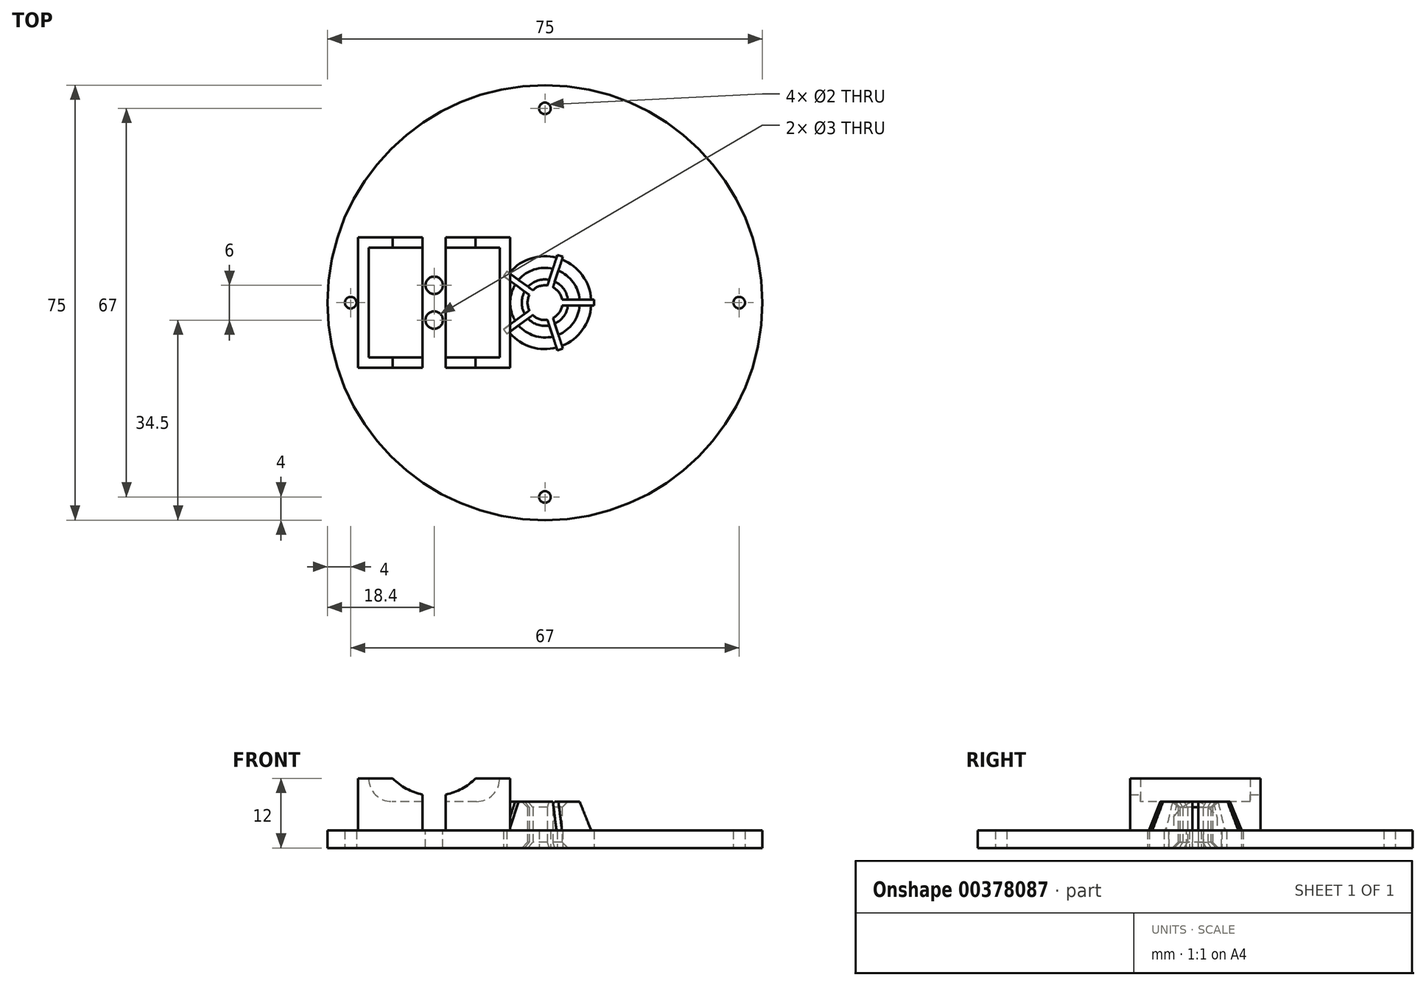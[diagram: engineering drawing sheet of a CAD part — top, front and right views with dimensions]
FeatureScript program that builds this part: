
annotation { "Feature Type Name" : "Feature", "Feature Type Description" : "" }
export const myFeature = defineFeature(function(context is Context, id is Id, definition is map)
    precondition{}
    {
        {
            var Q0;
            Q0=qCreatedBy(makeId("Top.planeOp"),FACE);
            var sketch = newSketch(context, id + "F0", { "sketchPlane" : qUnion([Q0])});
            skCircle(sketch, "E0", {"center": v(0, 0) * mm, "radius": 37.5 * mm});
            skCircle(sketch, "E1", {"center": v(0, 0) * mm, "radius": 3 * mm});
            skLineSegment(sketch, "E2.bottom", {"start": v(-8, 9.25) * mm, "end": v(-30.2, 9.25) * mm, "construction": true});
            skLineSegment(sketch, "E2.top", {"start": v(-8, -9.25) * mm, "end": v(-30.2, -9.25) * mm, "construction": true});
            skLineSegment(sketch, "E2.left", {"start": v(-8, 9.25) * mm, "end": v(-8, -9.25) * mm, "construction": true});
            skLineSegment(sketch, "E2.right", {"start": v(-30.2, 9.25) * mm, "end": v(-30.2, -9.25) * mm, "construction": true});
            skPoint(sketch, "E2.middle", {"position": v(-19.1, 0) * mm});
            skLineSegment(sketch, "E3", {"start": v(-3, 37.38) * mm, "end": v(-3, -37.38) * mm, "construction": true});
            skCircle(sketch, "E4", {"center": v(0, 0) * mm, "radius": 33.5 * mm, "construction": true});
            skCircle(sketch, "E5", {"center": v(33.5, 0) * mm, "radius": 1 * mm});
            skCircle(sketch, "E6.1.0", {"center": v(0, -33.5) * mm, "radius": 1 * mm});
            skCircle(sketch, "E6.2.0", {"center": v(-33.5, 0) * mm, "radius": 1 * mm});
            skCircle(sketch, "E6.3.0", {"center": v(0, 33.5) * mm, "radius": 1 * mm});
            skLineSegment(sketch, "E6.anchor1", {"start": v(0, 0) * mm, "end": v(33.5, 0) * mm, "construction": true});
            skLineSegment(sketch, "E6.anchor2", {"start": v(0, 0) * mm, "end": v(0, 33.5) * mm, "construction": true});
            skSolve(sketch);
        }
        {
            var Q0;
            Q0=makeQuery(id+"F0.imprint","IMPRINT",FACE,{"disambiguationData":[TD([[makeQuery(id+"F0.imprint","IMPRINT",EDGE,{"derivedFrom":sQuery(id+"F0.wireOp",EDGE,"E1")}),-1.0]])]});
            extrude(context, id + "F1", {"entities" : qUnion([Q0]), "depth" : 3 * mm});
        }
        {
            var Q0;
            Q0=makeQuery(id+"F1.opExtrude","CAP_FACE",FACE,{"disambiguationData":[OSD([sQuery(id+"F0.wireOp",EDGE,"E1"),sQuery(id+"F0.wireOp",EDGE,"E5"),sQuery(id+"F0.wireOp",EDGE,"E6.1.0"),sQuery(id+"F0.wireOp",EDGE,"E6.2.0"),sQuery(id+"F0.wireOp",EDGE,"E6.3.0"),sQuery(id+"F0.wireOp",EDGE,"E0")])],"isStart":false});
            var sketch = newSketch(context, id + "F2", { "sketchPlane" : qUnion([Q0])});
            skCircle(sketch, "E7", {"center": v(0, 0) * mm, "radius": 8 * mm});
            skCircle(sketch, "E8", {"center": v(0, 0) * mm, "radius": 3 * mm});
            skSolve(sketch);
        }
        {
            var Q0;
            Q0=makeQuery(id+"F2.imprint","IMPRINT",FACE,{"disambiguationData":[TD([[makeQuery(id+"F2.imprint","IMPRINT",EDGE,{"derivedFrom":sQuery(id+"F2.wireOp",EDGE,"E7")}),1.0]])]});
            extrude(context, id + "F3", {"entities" : qUnion([Q0]), "operationType" : NewBodyOperationType.ADD, "depth" : 5 * mm});
        }
        {
            var Q0;
            Q0=makeQuery(id+"F3.opExtrude","CAP_EDGE",EDGE,{"disambiguationData":[OSD([sQuery(id+"F2.wireOp",EDGE,"E7")])],"isStart":false});
            chamfer(context, id + "F4", {"entities" : qUnion([Q0]), "chamferType" : ChamferType.TWO_OFFSETS, "width1" : 2 * mm, "oppositeDirection" : false, "width2" : 5 * mm, "tangentPropagation" : true});
        }
        {
            var Q0;
            Q0=makeQuery(id+"F3.boolean.opBoolean","MERGE",FACE,{"derivedFrom":[makeQuery(id+"F1.opExtrude","SWEPT_FACE",FACE,{"disambiguationData":[OSD([sQuery(id+"F0.wireOp",EDGE,"E1")])]}),makeQuery(id+"F3.opExtrude","SWEPT_FACE",FACE,{"disambiguationData":[OSD([sQuery(id+"F2.wireOp",EDGE,"E8")])]})]});
            chamfer(context, id + "F5", {"entities" : qUnion([Q0]), "width" : 1 * mm, "tangentPropagation" : true});
        }
        {
            var Q0;
            Q0=makeQuery(id+"F1.opExtrude","CAP_FACE",FACE,{"disambiguationData":[OSD([sQuery(id+"F0.wireOp",EDGE,"E1"),sQuery(id+"F0.wireOp",EDGE,"E5"),sQuery(id+"F0.wireOp",EDGE,"E6.1.0"),sQuery(id+"F0.wireOp",EDGE,"E6.2.0"),sQuery(id+"F0.wireOp",EDGE,"E6.3.0"),sQuery(id+"F0.wireOp",EDGE,"E0")])],"isStart":true});
            var sketch = newSketch(context, id + "F6", { "sketchPlane" : qUnion([Q0])});
            skLineSegment(sketch, "E9.bottom", {"start": v(8.5, 0.5) * mm, "end": v(2.5, 0.5) * mm});
            skLineSegment(sketch, "E9.top", {"start": v(8.5, -0.5) * mm, "end": v(2.5, -0.5) * mm});
            skLineSegment(sketch, "E9.left", {"start": v(8.5, 0.5) * mm, "end": v(8.5, -0.5) * mm});
            skLineSegment(sketch, "E9.right", {"start": v(2.5, 0.5) * mm, "end": v(2.5, -0.5) * mm});
            skPoint(sketch, "E9.middle", {"position": v(5.5, 0) * mm});
            skLineSegment(sketch, "E10.1.0", {"start": v(3.1, 7.93) * mm, "end": v(1.25, 2.22) * mm});
            skLineSegment(sketch, "E10.1.1", {"start": v(2.15, 8.24) * mm, "end": v(3.1, 7.93) * mm});
            skLineSegment(sketch, "E10.1.2", {"start": v(2.15, 8.24) * mm, "end": v(0.3, 2.53) * mm});
            skLineSegment(sketch, "E10.1.3", {"start": v(0.3, 2.53) * mm, "end": v(1.25, 2.22) * mm});
            skLineSegment(sketch, "E10.2.0", {"start": v(-6.58, 5.4) * mm, "end": v(-1.73, 1.87) * mm});
            skLineSegment(sketch, "E10.2.1", {"start": v(-7.17, 4.6) * mm, "end": v(-6.58, 5.4) * mm});
            skLineSegment(sketch, "E10.2.2", {"start": v(-7.17, 4.6) * mm, "end": v(-2.32, 1.06) * mm});
            skLineSegment(sketch, "E10.2.3", {"start": v(-2.32, 1.06) * mm, "end": v(-1.73, 1.87) * mm});
            skLineSegment(sketch, "E10.3.0", {"start": v(-7.17, -4.6) * mm, "end": v(-2.32, -1.06) * mm});
            skLineSegment(sketch, "E10.3.1", {"start": v(-6.58, -5.4) * mm, "end": v(-7.17, -4.6) * mm});
            skLineSegment(sketch, "E10.3.2", {"start": v(-6.58, -5.4) * mm, "end": v(-1.73, -1.87) * mm});
            skLineSegment(sketch, "E10.3.3", {"start": v(-1.73, -1.87) * mm, "end": v(-2.32, -1.06) * mm});
            skLineSegment(sketch, "E10.4.0", {"start": v(2.15, -8.24) * mm, "end": v(0.3, -2.53) * mm});
            skLineSegment(sketch, "E10.4.1", {"start": v(3.1, -7.93) * mm, "end": v(2.15, -8.24) * mm});
            skLineSegment(sketch, "E10.4.2", {"start": v(3.1, -7.93) * mm, "end": v(1.25, -2.22) * mm});
            skLineSegment(sketch, "E10.4.3", {"start": v(1.25, -2.22) * mm, "end": v(0.3, -2.53) * mm});
            skPoint(sketch, "E10.center", {"position": v(0, 0) * mm});
            skSolve(sketch);
        }
        {
            var Q0;
            {var subQ0=sQuery(id+"F6.wireOp",EDGE,"E10.2.3");Q0=makeQuery(id+"F6.imprint","IMPRINT",FACE,{"disambiguationData":[TD([[makeQuery(id+"F6.imprint","IMPRINT",EDGE,{"derivedFrom":subQ0}),1.0]])]});}
            var Q1;
            {var subQ0=sQuery(id+"F6.wireOp",EDGE,"E10.1.3");Q1=makeQuery(id+"F6.imprint","IMPRINT",FACE,{"disambiguationData":[TD([[makeQuery(id+"F6.imprint","IMPRINT",EDGE,{"derivedFrom":subQ0}),1.0]])]});}
            var Q2;
            {var subQ0=sQuery(id+"F6.wireOp",EDGE,"E10.1.1");Q2=makeQuery(id+"F6.imprint","IMPRINT",FACE,{"disambiguationData":[TD([[makeQuery(id+"F6.imprint","IMPRINT",EDGE,{"derivedFrom":subQ0}),-1.0]])]});}
            var Q3;
            {var subQ0=sQuery(id+"F6.wireOp",EDGE,"E9.left");Q3=makeQuery(id+"F6.imprint","IMPRINT",FACE,{"disambiguationData":[TD([[makeQuery(id+"F6.imprint","IMPRINT",EDGE,{"derivedFrom":subQ0}),-1.0]])]});}
            var Q4;
            {var subQ0=sQuery(id+"F6.wireOp",EDGE,"E10.4.1");Q4=makeQuery(id+"F6.imprint","IMPRINT",FACE,{"disambiguationData":[TD([[makeQuery(id+"F6.imprint","IMPRINT",EDGE,{"derivedFrom":subQ0}),-1.0]])]});}
            var Q5;
            {var subQ0=sQuery(id+"F6.wireOp",EDGE,"E9.right");Q5=makeQuery(id+"F6.imprint","IMPRINT",FACE,{"disambiguationData":[TD([[makeQuery(id+"F6.imprint","IMPRINT",EDGE,{"derivedFrom":subQ0}),1.0]])]});}
            var Q6;
            {var subQ0=sQuery(id+"F6.wireOp",EDGE,"E10.4.3");Q6=makeQuery(id+"F6.imprint","IMPRINT",FACE,{"disambiguationData":[TD([[makeQuery(id+"F6.imprint","IMPRINT",EDGE,{"derivedFrom":subQ0}),1.0]])]});}
            var Q7;
            {var subQ0=sQuery(id+"F6.wireOp",EDGE,"E10.3.1");Q7=makeQuery(id+"F6.imprint","IMPRINT",FACE,{"disambiguationData":[TD([[makeQuery(id+"F6.imprint","IMPRINT",EDGE,{"derivedFrom":subQ0}),-1.0]])]});}
            var Q8;
            {var subQ0=sQuery(id+"F6.wireOp",EDGE,"E10.3.3");Q8=makeQuery(id+"F6.imprint","IMPRINT",FACE,{"disambiguationData":[TD([[makeQuery(id+"F6.imprint","IMPRINT",EDGE,{"derivedFrom":subQ0}),1.0]])]});}
            var Q9;
            {var subQ0=sQuery(id+"F6.wireOp",EDGE,"E10.2.1");Q9=makeQuery(id+"F6.imprint","IMPRINT",FACE,{"disambiguationData":[TD([[makeQuery(id+"F6.imprint","IMPRINT",EDGE,{"derivedFrom":subQ0}),-1.0]])]});}
            extrude(context, id + "F7", {"entities" : qUnion([Q0, Q1, Q2, Q3, Q4, Q5, Q6, Q7, Q8, Q9]), "operationType" : NewBodyOperationType.REMOVE, "endBound" : BoundingType.THROUGH_ALL, "oppositeDirection" : true, "depth" : 25 * mm});
        }
        {
            var Q0;
            Q0=makeQuery(id+"F1.opExtrude","CAP_FACE",FACE,{"disambiguationData":[OSD([sQuery(id+"F0.wireOp",EDGE,"E1"),sQuery(id+"F0.wireOp",EDGE,"E5"),sQuery(id+"F0.wireOp",EDGE,"E6.1.0"),sQuery(id+"F0.wireOp",EDGE,"E6.2.0"),sQuery(id+"F0.wireOp",EDGE,"E6.3.0"),sQuery(id+"F0.wireOp",EDGE,"E0")])],"isStart":false});
            var sketch = newSketch(context, id + "F8", { "sketchPlane" : qUnion([Q0])});
            skLineSegment(sketch, "E11", {"start": v(-19.1, 3) * mm, "end": v(-19.1, -3) * mm, "construction": true});
            skCircle(sketch, "E12", {"center": v(-19.1, 3) * mm, "radius": 1.5 * mm});
            skCircle(sketch, "E13", {"center": v(-19.1, -3) * mm, "radius": 1.5 * mm});
            skSolve(sketch);
        }
        {
            var Q0;
            Q0 = qSketchRegion(id + "F8", true);
            extrude(context, id + "F9", {"entities" : qUnion([Q0]), "operationType" : NewBodyOperationType.REMOVE, "endBound" : BoundingType.THROUGH_ALL, "oppositeDirection" : true, "depth" : 25 * mm});
        }
        {
            var Q0;
            Q0=makeQuery(id+"F8.imprint","IMPRINT",FACE,{"disambiguationData":[TD([[makeQuery(id+"F8.imprint","IMPRINT",EDGE,{"derivedFrom":sQuery(id+"F8.wireOp",EDGE,"E12")}),-1.0]])]});
            var sketch = newSketch(context, id + "F10", { "sketchPlane" : qUnion([Q0])});
            skLineSegment(sketch, "E14.0", {"start": v(-6, 11.25) * mm, "end": v(-32.2, 11.25) * mm});
            skLineSegment(sketch, "E14.1", {"start": v(-6, 11.25) * mm, "end": v(-6, -11.25) * mm});
            skLineSegment(sketch, "E14.2", {"start": v(-6, -11.25) * mm, "end": v(-32.2, -11.25) * mm});
            skLineSegment(sketch, "E14.3", {"start": v(-32.2, 11.25) * mm, "end": v(-32.2, -11.25) * mm});
            skSolve(sketch);
        }
        {
            var Q0;
            Q0 = qSketchRegion(id + "F10", true);
            extrude(context, id + "F11", {"entities" : qUnion([Q0]), "operationType" : NewBodyOperationType.ADD, "depth" : 9 * mm});
        }
        {
            var Q0;
            Q0=makeQuery(id+"F11.opExtrude","CAP_FACE",FACE,{"disambiguationData":[OSD([sQuery(id+"F10.wireOp",EDGE,"E14.0"),sQuery(id+"F10.wireOp",EDGE,"E14.1"),sQuery(id+"F10.wireOp",EDGE,"E14.2"),sQuery(id+"F10.wireOp",EDGE,"E14.3")])],"isStart":false});
            var sketch = newSketch(context, id + "F12", { "sketchPlane" : qUnion([Q0])});
            skLineSegment(sketch, "E15.0", {"start": v(-7.8, 9.45) * mm, "end": v(-30.4, 9.45) * mm});
            skLineSegment(sketch, "E15.1", {"start": v(-7.8, 9.45) * mm, "end": v(-7.8, -9.45) * mm});
            skLineSegment(sketch, "E15.2", {"start": v(-7.8, -9.45) * mm, "end": v(-30.4, -9.45) * mm});
            skLineSegment(sketch, "E15.3", {"start": v(-30.4, 9.45) * mm, "end": v(-30.4, -9.45) * mm});
            skSolve(sketch);
        }
        {
            var Q0;
            Q0 = qSketchRegion(id + "F12", true);
            extrude(context, id + "F13", {"entities" : qUnion([Q0]), "operationType" : NewBodyOperationType.REMOVE, "oppositeDirection" : true, "depth" : 4 * mm});
        }
        {
            var Q0;
            Q0=makeQuery(id+"F13.boolean.opBoolean","COPY",EDGE,{"derivedFrom":makeQuery(id+"F13.opExtrude","CAP_EDGE",EDGE,{"disambiguationData":[OSD([sQuery(id+"F12.wireOp",EDGE,"E15.3")])],"isStart":false})});
            var Q1;
            Q1=makeQuery(id+"F13.boolean.opBoolean","COPY",EDGE,{"derivedFrom":makeQuery(id+"F13.opExtrude","CAP_EDGE",EDGE,{"disambiguationData":[OSD([sQuery(id+"F12.wireOp",EDGE,"E15.1")])],"isStart":false})});
            fillet(context, id + "F14", {"entities" : qUnion([Q0, Q1]), "radius" : 4 * mm, "tangentPropagation" : true, "allowEdgeOverflow" : false});
        }
        {
            var Q0;
            Q0=makeQuery(id+"F11.opExtrude","CAP_FACE",FACE,{"disambiguationData":[OSD([sQuery(id+"F10.wireOp",EDGE,"E14.0"),sQuery(id+"F10.wireOp",EDGE,"E14.1"),sQuery(id+"F10.wireOp",EDGE,"E14.2"),sQuery(id+"F10.wireOp",EDGE,"E14.3")])],"isStart":false});
            var sketch = newSketch(context, id + "F15", { "sketchPlane" : qUnion([Q0])});
            skLineSegment(sketch, "E16.bottom", {"start": v(-21.1, 11.25) * mm, "end": v(-17.1, 11.25) * mm});
            skLineSegment(sketch, "E16.top", {"start": v(-21.1, -11.25) * mm, "end": v(-17.1, -11.25) * mm});
            skLineSegment(sketch, "E16.left", {"start": v(-21.1, 11.25) * mm, "end": v(-21.1, -11.25) * mm});
            skLineSegment(sketch, "E16.right", {"start": v(-17.1, 11.25) * mm, "end": v(-17.1, -11.25) * mm});
            skPoint(sketch, "E16.middle", {"position": v(-19.1, 0) * mm});
            skSolve(sketch);
        }
        {
            var Q0;
            Q0 = qSketchRegion(id + "F15", true);
            var Q1;
            Q1=makeQuery(id+"F1.opExtrude","CAP_FACE",FACE,{"disambiguationData":[OSD([sQuery(id+"F0.wireOp",EDGE,"E1"),sQuery(id+"F0.wireOp",EDGE,"E5"),sQuery(id+"F0.wireOp",EDGE,"E6.1.0"),sQuery(id+"F0.wireOp",EDGE,"E6.2.0"),sQuery(id+"F0.wireOp",EDGE,"E6.3.0"),sQuery(id+"F0.wireOp",EDGE,"E0")])],"isStart":false});
            extrude(context, id + "F16", {"entities" : qUnion([Q0]), "operationType" : NewBodyOperationType.REMOVE, "endBound" : BoundingType.UP_TO_SURFACE, "oppositeDirection" : true, "endBoundEntityFace" : qUnion([Q1]), "depth" : 25 * mm});
        }
        {
            var Q0;
            {var subQ0=sQuery(id+"F12.wireOp",EDGE,"E15.1");var subQ1=sQuery(id+"F12.wireOp",EDGE,"E15.0");Q0=makeQuery(id+"F16.boolean.opBoolean","SPLIT",FACE,{"disambiguationData":[TD([makeQuery(id+"F14.opFillet","BLEND_FACE",FACE,{"disambiguationData":[OSD([subQ0])]})])],"derivedFrom":makeQuery(id+"F13.boolean.opBoolean","COPY",FACE,{"derivedFrom":makeQuery(id+"F13.opExtrude","SWEPT_FACE",FACE,{"disambiguationData":[OSD([subQ1])]})})});}
            var sketch = newSketch(context, id + "F17", { "sketchPlane" : qUnion([Q0])});
            skLineSegment(sketch, "E17", {"start": v(-17.1, 8) * mm, "end": v(-21.1, 8) * mm, "construction": true});
            skCircle(sketch, "E18", {"center": v(-19.1, 19) * mm, "radius": 10 * mm});
            skLineSegment(sketch, "E19", {"start": v(-19.1, 19) * mm, "end": v(-19.1, 8) * mm, "construction": true});
            skSolve(sketch);
        }
        {
            var Q0;
            {var subQ0=sQuery(id+"F17.wireOp",EDGE,"E18");var subQ1=sQuery(id+"F12.wireOp",EDGE,"E15.0");var subQ2=makeQuery(id+"F13.boolean.opBoolean","COPY",FACE,{"derivedFrom":makeQuery(id+"F13.opExtrude","SWEPT_FACE",FACE,{"disambiguationData":[OSD([subQ1])]})});var subQ3=makeQuery(id+"F16.opExtrude","SWEPT_FACE",FACE,{"disambiguationData":[OSD([sQuery(id+"F15.wireOp",EDGE,"E16.right")])]});var subQ6=makeQuery(id+"F16.boolean.opBoolean","INTERSECT",EDGE,{"derivedFrom":[subQ2,subQ3]});var subQ7=makeQuery(id+"F17.imprint","INTERSECT",VERTEX,{"derivedFrom":[subQ6,subQ0]});Q0=makeQuery(id+"F17.imprint","IMPRINT",FACE,{"disambiguationData":[TD([[makeQuery(id+"F17.imprint","IMPRINT",EDGE,{"disambiguationData":[TD([[subQ7,1.0]])],"derivedFrom":subQ0}),1.0]])]});}
            var Q1;
            {var subQ0=sQuery(id+"F17.wireOp",EDGE,"E18");var subQ1=sQuery(id+"F12.wireOp",EDGE,"E15.0");var subQ2=makeQuery(id+"F13.boolean.opBoolean","COPY",FACE,{"derivedFrom":makeQuery(id+"F13.opExtrude","SWEPT_FACE",FACE,{"disambiguationData":[OSD([subQ1])]})});var subQ3=makeQuery(id+"F16.opExtrude","SWEPT_FACE",FACE,{"disambiguationData":[OSD([sQuery(id+"F15.wireOp",EDGE,"E16.right")])]});var subQ6=makeQuery(id+"F16.boolean.opBoolean","INTERSECT",EDGE,{"derivedFrom":[subQ2,subQ3]});var subQ7=makeQuery(id+"F17.imprint","INTERSECT",VERTEX,{"derivedFrom":[subQ6,subQ0]});Q1=makeQuery(id+"F17.imprint","IMPRINT",FACE,{"disambiguationData":[TD([[makeQuery(id+"F17.imprint","IMPRINT",EDGE,{"disambiguationData":[TD([[subQ7,-1.0]])],"derivedFrom":subQ0}),1.0]])]});}
            var Q2;
            Q2=sQuery(id+"F17.wireOp",EDGE,"E18");
            extrude(context, id + "F18", {"entities" : qUnion([Q0, Q1]), "operationType" : NewBodyOperationType.REMOVE, "surfaceEntities" : qUnion([Q2]), "endBound" : BoundingType.SYMMETRIC, "depth" : 50 * mm});
        }
    });
